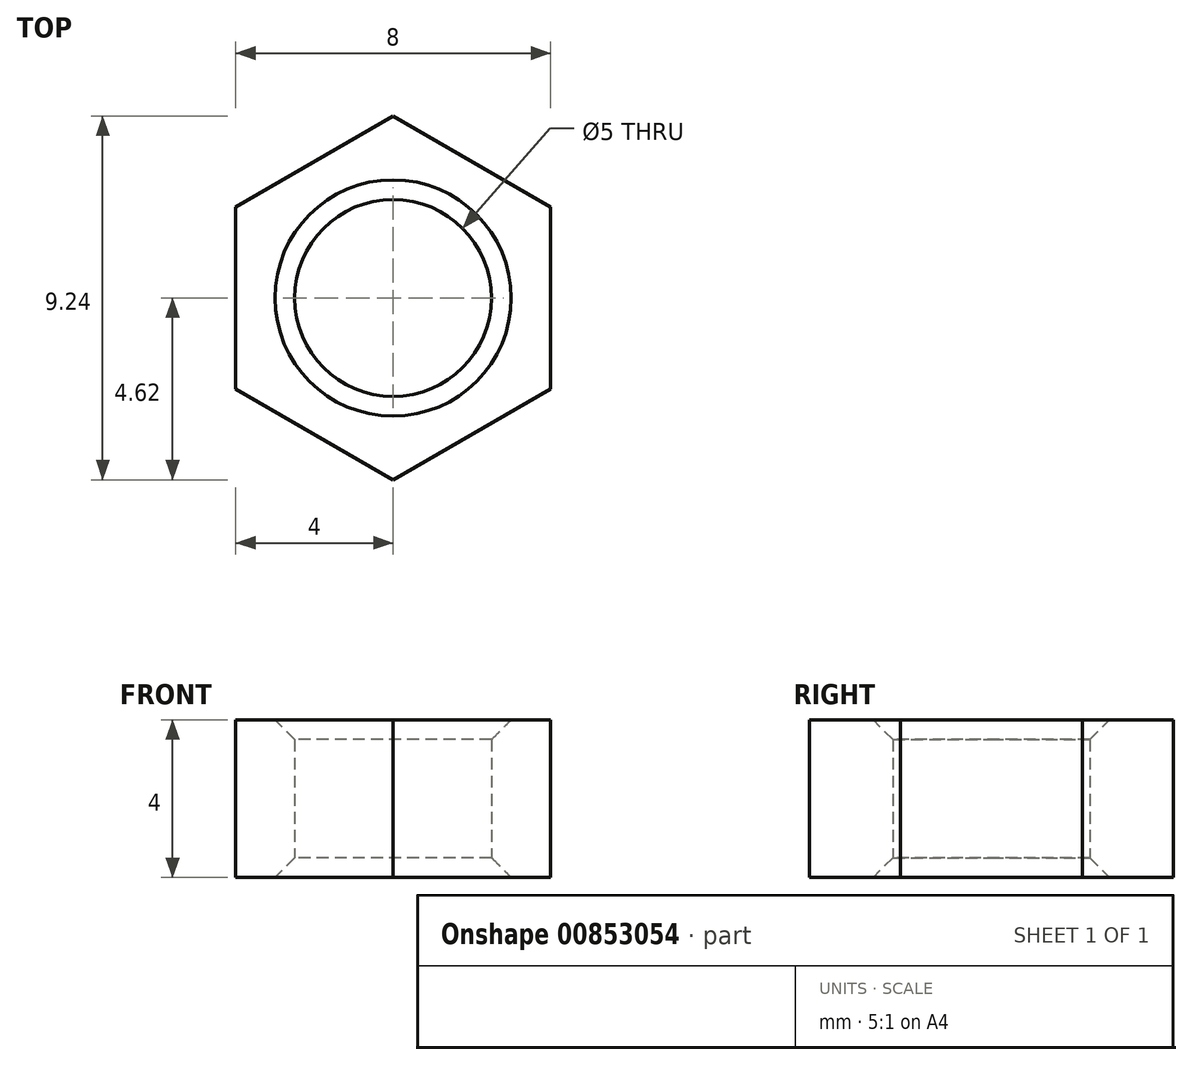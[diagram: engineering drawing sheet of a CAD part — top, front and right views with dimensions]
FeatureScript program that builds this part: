
annotation { "Feature Type Name" : "Feature", "Feature Type Description" : "" }
export const myFeature = defineFeature(function(context is Context, id is Id, definition is map)
    precondition{}
    {
        {
            var Q0;
            Q0=qCreatedBy(makeId("Top.planeOp"),FACE);
            var sketch = newSketch(context, id + "F0", { "sketchPlane" : qUnion([Q0])});
            skCircle(sketch, "E0", {"center": v(0, 0) * mm, "radius": 2.5 * mm});
            skCircle(sketch, "E1.cCircle", {"center": v(0, 0) * mm, "radius": 4 * mm, "construction": true});
            skLineSegment(sketch, "E1.0", {"start": v(4, 2.3) * mm, "end": v(4, -2.3) * mm});
            skLineSegment(sketch, "E1.1", {"start": v(4, -2.3) * mm, "end": v(0, -4.62) * mm});
            skLineSegment(sketch, "E1.2", {"start": v(0, -4.62) * mm, "end": v(-4, -2.3) * mm});
            skLineSegment(sketch, "E1.3", {"start": v(-4, -2.3) * mm, "end": v(-4, 2.3) * mm});
            skLineSegment(sketch, "E1.4", {"start": v(-4, 2.3) * mm, "end": v(0, 4.62) * mm});
            skLineSegment(sketch, "E1.5", {"start": v(0, 4.62) * mm, "end": v(4, 2.3) * mm});
            skPoint(sketch, "E1.0.midPoint", {"position": v(4, 0) * mm});
            skSolve(sketch);
        }
        {
            var Q0;
            Q0 = qSketchRegion(id + "F0", true);
            extrude(context, id + "F1", {"entities" : qUnion([Q0]), "depth" : 4 * mm, "offsetDistance" : 25 * mm});
        }
        {
            var Q0;
            Q0=makeQuery(id+"F1.opExtrude","CAP_EDGE",EDGE,{"disambiguationData":[OSD([sQuery(id+"F0.wireOp",EDGE,"E0")])],"isStart":false});
            var Q1;
            Q1=makeQuery(id+"F1.opExtrude","CAP_EDGE",EDGE,{"disambiguationData":[OSD([sQuery(id+"F0.wireOp",EDGE,"E0")])],"isStart":true});
            chamfer(context, id + "F2", {"entities" : qUnion([Q0, Q1]), "width" : 0.5 * mm, "tangentPropagation" : true});
        }
    });
